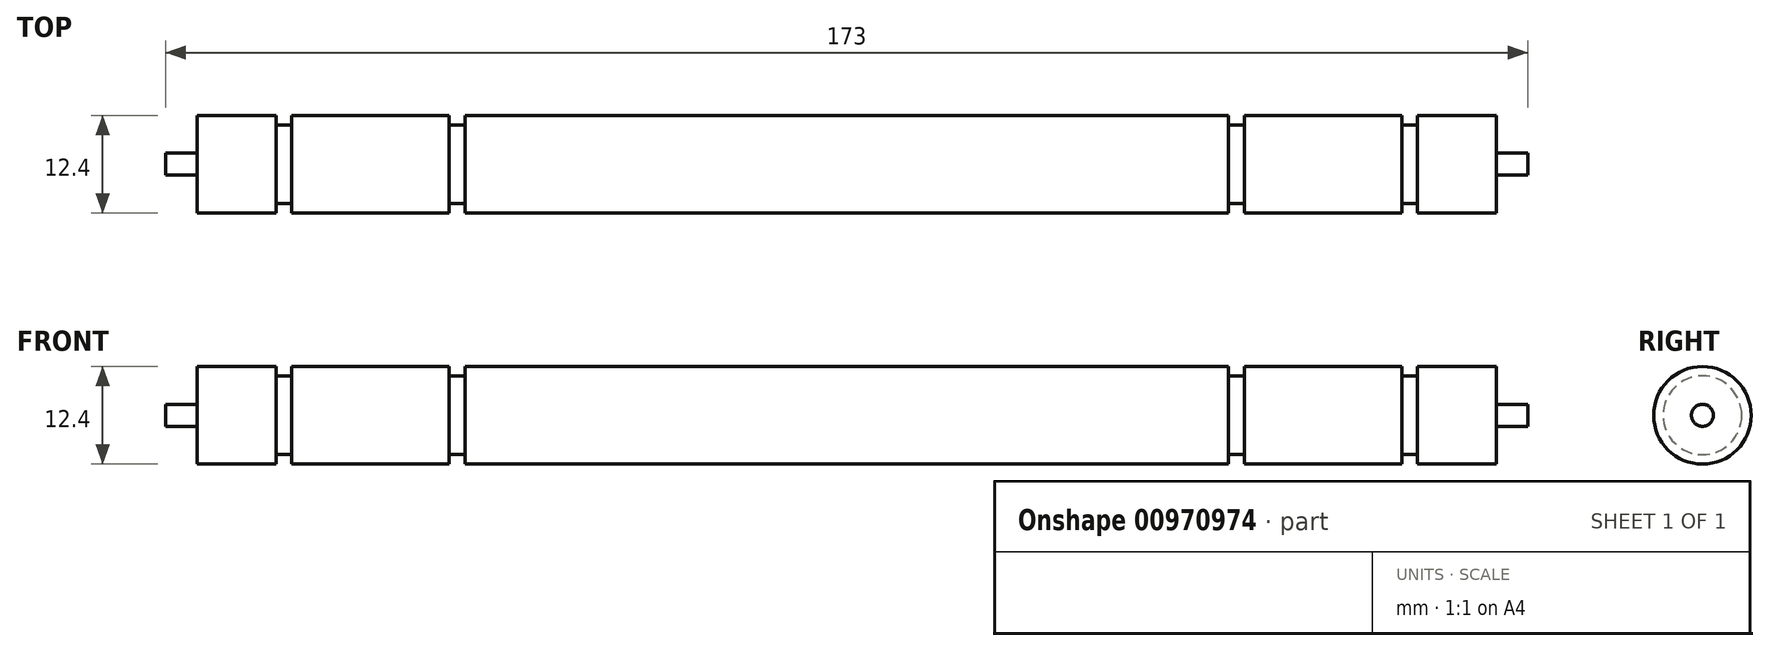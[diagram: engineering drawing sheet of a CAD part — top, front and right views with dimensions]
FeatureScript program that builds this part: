
annotation { "Feature Type Name" : "Feature", "Feature Type Description" : "" }
export const myFeature = defineFeature(function(context is Context, id is Id, definition is map)
    precondition{}
    {
        {
            var Q0;
            Q0=qCreatedBy(makeId("Front.planeOp"),FACE);
            var sketch = newSketch(context, id + "F0", { "sketchPlane" : qUnion([Q0])});
            skLineSegment(sketch, "E0", {"start": v(0, 0) * mm, "end": v(86.5, 0) * mm});
            skLineSegment(sketch, "E1", {"start": v(86.5, 0) * mm, "end": v(86.5, 1.4) * mm});
            skLineSegment(sketch, "E2", {"start": v(86.5, 1.4) * mm, "end": v(82.5, 1.4) * mm});
            skLineSegment(sketch, "E3", {"start": v(82.5, 1.4) * mm, "end": v(82.5, 6.2) * mm});
            skLineSegment(sketch, "E4", {"start": v(82.5, 6.2) * mm, "end": v(72.5, 6.2) * mm});
            skLineSegment(sketch, "E5", {"start": v(72.5, 6.2) * mm, "end": v(72.5, 5) * mm});
            skLineSegment(sketch, "E6", {"start": v(72.5, 5) * mm, "end": v(70.5, 5) * mm});
            skLineSegment(sketch, "E7", {"start": v(70.5, 5) * mm, "end": v(70.5, 6.2) * mm});
            skLineSegment(sketch, "E8", {"start": v(70.5, 6.2) * mm, "end": v(0, 6.2) * mm});
            skLineSegment(sketch, "E9", {"start": v(0, 6.2) * mm, "end": v(0, 0) * mm});
            skLineSegment(sketch, "E10.bottom", {"start": v(50.5, 6.2) * mm, "end": v(48.5, 6.2) * mm});
            skLineSegment(sketch, "E10.top", {"start": v(50.5, 5) * mm, "end": v(48.5, 5) * mm});
            skLineSegment(sketch, "E10.left", {"start": v(50.5, 6.2) * mm, "end": v(50.5, 5) * mm});
            skLineSegment(sketch, "E10.right", {"start": v(48.5, 6.2) * mm, "end": v(48.5, 5) * mm});
            skSolve(sketch);
        }
        {
            var Q0;
            Q0=makeQuery(id+"F0.imprint","IMPRINT",FACE,{"disambiguationData":[TD([[makeQuery(id+"F0.imprint","IMPRINT",EDGE,{"derivedFrom":sQuery(id+"F0.wireOp",EDGE,"E0")}),1.0]])]});
            var Q1;
            Q1=sQuery(id+"F0.wireOp",EDGE,"E0");
            revolve(context, id + "F1", {"surfaceOperationType" : NewSurfaceOperationType.NEW, "entities" : qUnion([Q0]), "axis" : qUnion([Q1]), "revolveType" : RevolveType.FULL});
        }
        {
            var Q0;
            Q0=makeQuery(id+"F1.opRevolve","SWEPT_BODY",BODY,{"disambiguationData":[OSD([sQuery(id+"F0.wireOp",EDGE,"E0"),sQuery(id+"F0.wireOp",EDGE,"E1"),sQuery(id+"F0.wireOp",EDGE,"E2"),sQuery(id+"F0.wireOp",EDGE,"E3"),sQuery(id+"F0.wireOp",EDGE,"E4"),sQuery(id+"F0.wireOp",EDGE,"E5"),sQuery(id+"F0.wireOp",EDGE,"E6"),sQuery(id+"F0.wireOp",EDGE,"E7"),sQuery(id+"F0.wireOp",EDGE,"E8"),sQuery(id+"F0.wireOp",EDGE,"E9"),sQuery(id+"F0.wireOp",EDGE,"E10.top"),sQuery(id+"F0.wireOp",EDGE,"E10.left"),sQuery(id+"F0.wireOp",EDGE,"E10.right")])]});
            var Q1;
            Q1=makeQuery(id+"F1.opRevolve","SWEPT_FACE",FACE,{"disambiguationData":[OSD([sQuery(id+"F0.wireOp",EDGE,"E9")])]});
            mirror(context, id + "F2", {"operationType" : NewBodyOperationType.ADD, "entities" : qUnion([Q0]), "mirrorPlane" : qUnion([Q1])});
        }
    });
